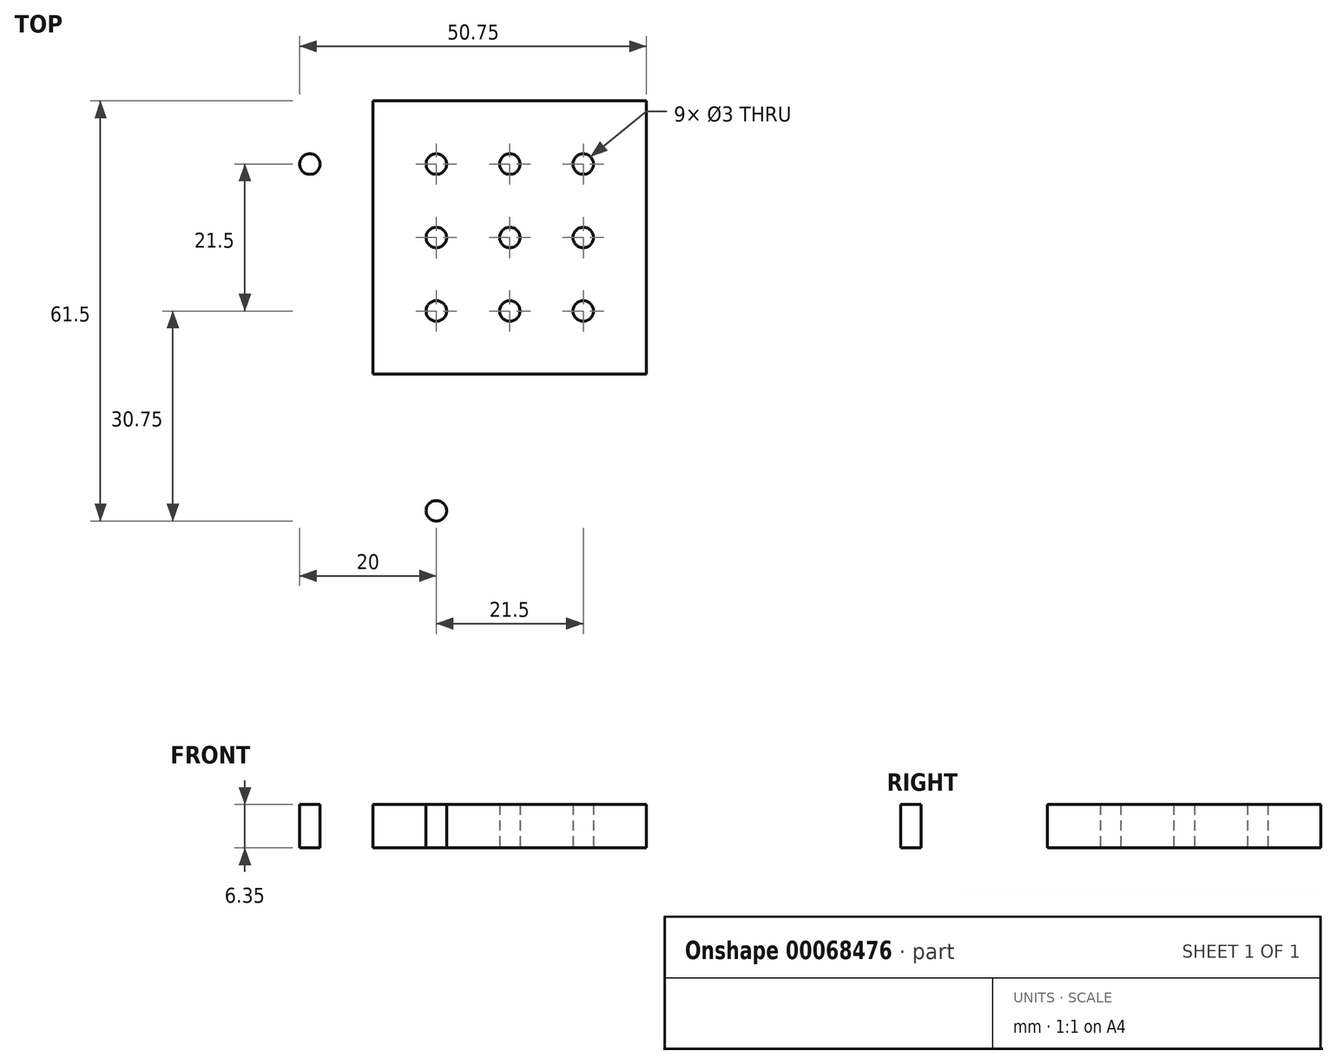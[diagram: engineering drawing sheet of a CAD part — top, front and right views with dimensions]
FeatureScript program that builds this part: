
annotation { "Feature Type Name" : "Feature", "Feature Type Description" : "" }
export const myFeature = defineFeature(function(context is Context, id is Id, definition is map)
    precondition{}
    {
        {
            var Q0;
            Q0=qCreatedBy(makeId("Top.planeOp"),FACE);
            var sketch = newSketch(context, id + "F0", { "sketchPlane" : qUnion([Q0])});
            skLineSegment(sketch, "E0.bottom", {"start": v(9.25, 0) * mm, "end": v(40, 0) * mm});
            skLineSegment(sketch, "E0.top", {"start": v(0, 40) * mm, "end": v(40, 40) * mm});
            skLineSegment(sketch, "E0.left", {"start": v(0, 0) * mm, "end": v(0, 40) * mm});
            skLineSegment(sketch, "E0.right", {"start": v(40, 0) * mm, "end": v(40, 40) * mm});
            skCircle(sketch, "E1", {"center": v(9.25, 30.75) * mm, "radius": 1.5 * mm});
            skCircle(sketch, "E2", {"center": v(20, 30.75) * mm, "radius": 1.5 * mm});
            skCircle(sketch, "E3", {"center": v(30.75, 30.75) * mm, "radius": 1.5 * mm});
            skCircle(sketch, "E4", {"center": v(9.25, 20) * mm, "radius": 1.5 * mm});
            skCircle(sketch, "E5", {"center": v(20, 20) * mm, "radius": 1.5 * mm});
            skCircle(sketch, "E6", {"center": v(30.75, 20) * mm, "radius": 1.5 * mm});
            skCircle(sketch, "E7", {"center": v(9.25, 9.25) * mm, "radius": 1.5 * mm});
            skCircle(sketch, "E8", {"center": v(20, 9.25) * mm, "radius": 1.5 * mm});
            skCircle(sketch, "E9", {"center": v(30.75, 9.25) * mm, "radius": 1.5 * mm});
            skLineSegment(sketch, "E10", {"start": v(0, 30.75) * mm, "end": v(7.75, 30.75) * mm, "construction": true});
            skLineSegment(sketch, "E11", {"start": v(9.25, 40) * mm, "end": v(9.25, 32.25) * mm, "construction": true});
            skLineSegment(sketch, "E12.trimOffspring", {"start": v(9.25, 29.25) * mm, "end": v(9.25, 21.5) * mm, "construction": true});
            skLineSegment(sketch, "E13.trimOffspring", {"start": v(10.75, 30.75) * mm, "end": v(18.5, 30.75) * mm, "construction": true});
            skLineSegment(sketch, "E14.trimOffspring", {"start": v(21.5, 30.75) * mm, "end": v(29.25, 30.75) * mm, "construction": true});
            skLineSegment(sketch, "E15.trimOffspring", {"start": v(32.25, 30.75) * mm, "end": v(40, 30.75) * mm, "construction": true});
            skLineSegment(sketch, "E16.trimOffspring", {"start": v(9.25, 18.5) * mm, "end": v(9.25, 10.75) * mm, "construction": true});
            skLineSegment(sketch, "E17.trimOffspring", {"start": v(9.25, 7.75) * mm, "end": v(9.25, 0) * mm, "construction": true});
            skCircle(sketch, "E18.MirrorC", {"center": v(-9.25, 30.75) * mm, "radius": 1.5 * mm});
            skCircle(sketch, "E19.MirrorC", {"center": v(-9.25, 9.25) * mm, "radius": 1.5 * mm});
            skCircle(sketch, "E20.MirrorC", {"center": v(-30.75, 30.75) * mm, "radius": 1.5 * mm});
            skCircle(sketch, "E21.MirrorC", {"center": v(-20, 30.75) * mm, "radius": 1.5 * mm});
            skCircle(sketch, "E22.MirrorC", {"center": v(-30.75, 9.25) * mm, "radius": 1.5 * mm});
            skCircle(sketch, "E23.MirrorC", {"center": v(-9.25, 20) * mm, "radius": 1.5 * mm});
            skCircle(sketch, "E24.MirrorC", {"center": v(-20, 9.25) * mm, "radius": 1.5 * mm});
            skCircle(sketch, "E25.MirrorC", {"center": v(-30.75, 20) * mm, "radius": 1.5 * mm});
            skCircle(sketch, "E26.MirrorC", {"center": v(-20, 20) * mm, "radius": 1.5 * mm});
            skLineSegment(sketch, "E27.MirrorCS", {"start": v(-10.75, 30.75) * mm, "end": v(-18.5, 30.75) * mm, "construction": true});
            skLineSegment(sketch, "E28.MirrorCS", {"start": v(-32.25, 30.75) * mm, "end": v(-40, 30.75) * mm, "construction": true});
            skLineSegment(sketch, "E29.MirrorCS", {"start": v(0, 30.75) * mm, "end": v(-7.75, 30.75) * mm, "construction": true});
            skLineSegment(sketch, "E30.MirrorCS", {"start": v(-40, 0) * mm, "end": v(-40, 40) * mm});
            skLineSegment(sketch, "E31.MirrorCS", {"start": v(-21.5, 30.75) * mm, "end": v(-29.25, 30.75) * mm, "construction": true});
            skLineSegment(sketch, "E32.MirrorCS", {"start": v(-9.25, 29.25) * mm, "end": v(-9.25, 21.5) * mm, "construction": true});
            skLineSegment(sketch, "E33.MirrorCS", {"start": v(-9.25, 40) * mm, "end": v(-9.25, 32.25) * mm, "construction": true});
            skLineSegment(sketch, "E34.MirrorCS", {"start": v(0, 40) * mm, "end": v(-40, 40) * mm});
            skLineSegment(sketch, "E35.MirrorCS", {"start": v(-9.25, 18.5) * mm, "end": v(-9.25, 10.75) * mm, "construction": true});
            skCircle(sketch, "E36.MirrorC", {"center": v(-9.25, -9.25) * mm, "radius": 1.5 * mm});
            skCircle(sketch, "E37.MirrorC", {"center": v(9.25, -20) * mm, "radius": 1.5 * mm});
            skCircle(sketch, "E38.MirrorC", {"center": v(9.25, -30.75) * mm, "radius": 1.5 * mm});
            skCircle(sketch, "E39.MirrorC", {"center": v(-30.75, -9.25) * mm, "radius": 1.5 * mm});
            skCircle(sketch, "E40.MirrorC", {"center": v(-9.25, -30.75) * mm, "radius": 1.5 * mm});
            skCircle(sketch, "E41.MirrorC", {"center": v(-20, -30.75) * mm, "radius": 1.5 * mm});
            skCircle(sketch, "E42.MirrorC", {"center": v(-30.75, -20) * mm, "radius": 1.5 * mm});
            skCircle(sketch, "E43.MirrorC", {"center": v(-20, -20) * mm, "radius": 1.5 * mm});
            skCircle(sketch, "E44.MirrorC", {"center": v(-30.75, -30.75) * mm, "radius": 1.5 * mm});
            skCircle(sketch, "E45.MirrorC", {"center": v(30.75, -9.25) * mm, "radius": 1.5 * mm});
            skCircle(sketch, "E46.MirrorC", {"center": v(30.75, -30.75) * mm, "radius": 1.5 * mm});
            skCircle(sketch, "E47.MirrorC", {"center": v(20, -20) * mm, "radius": 1.5 * mm});
            skCircle(sketch, "E48.MirrorC", {"center": v(-20, -9.25) * mm, "radius": 1.5 * mm});
            skCircle(sketch, "E49.MirrorC", {"center": v(20, -9.25) * mm, "radius": 1.5 * mm});
            skCircle(sketch, "E50.MirrorC", {"center": v(30.75, -20) * mm, "radius": 1.5 * mm});
            skLineSegment(sketch, "E51.MirrorCS", {"start": v(0, 0) * mm, "end": v(0, -40) * mm, "construction": true});
            skCircle(sketch, "E52.MirrorC", {"center": v(20, -30.75) * mm, "radius": 1.5 * mm});
            skCircle(sketch, "E53.MirrorC", {"center": v(-9.25, -20) * mm, "radius": 1.5 * mm});
            skCircle(sketch, "E54.MirrorC", {"center": v(9.25, -9.25) * mm, "radius": 1.5 * mm});
            skLineSegment(sketch, "E55.MirrorCS", {"start": v(-40, 0) * mm, "end": v(-40, -40) * mm});
            skLineSegment(sketch, "E56.MirrorCS", {"start": v(32.25, -30.75) * mm, "end": v(40, -30.75) * mm, "construction": true});
            skLineSegment(sketch, "E57.MirrorCS", {"start": v(-32.25, -30.75) * mm, "end": v(-40, -30.75) * mm, "construction": true});
            skLineSegment(sketch, "E58.MirrorCS", {"start": v(-9.25, -40) * mm, "end": v(-9.25, -32.25) * mm, "construction": true});
            skLineSegment(sketch, "E59.MirrorCS", {"start": v(21.5, -30.75) * mm, "end": v(29.25, -30.75) * mm, "construction": true});
            skLineSegment(sketch, "E60.MirrorCS", {"start": v(-10.75, -30.75) * mm, "end": v(-18.5, -30.75) * mm, "construction": true});
            skLineSegment(sketch, "E61.MirrorCS", {"start": v(-9.25, -29.25) * mm, "end": v(-9.25, -21.5) * mm, "construction": true});
            skLineSegment(sketch, "E62.MirrorCS", {"start": v(-9.25, -18.5) * mm, "end": v(-9.25, -10.75) * mm, "construction": true});
            skLineSegment(sketch, "E63.MirrorCS", {"start": v(0, -30.75) * mm, "end": v(-7.75, -30.75) * mm, "construction": true});
            skLineSegment(sketch, "E64.MirrorCS", {"start": v(10.75, -30.75) * mm, "end": v(18.5, -30.75) * mm, "construction": true});
            skLineSegment(sketch, "E65.MirrorCS", {"start": v(-21.5, -30.75) * mm, "end": v(-29.25, -30.75) * mm, "construction": true});
            skLineSegment(sketch, "E66.MirrorCS", {"start": v(9.25, -7.75) * mm, "end": v(9.25, 0) * mm, "construction": true});
            skLineSegment(sketch, "E67.MirrorCS", {"start": v(0, -40) * mm, "end": v(-40, -40) * mm});
            skLineSegment(sketch, "E68.MirrorCS", {"start": v(9.25, -40) * mm, "end": v(9.25, -32.25) * mm, "construction": true});
            skLineSegment(sketch, "E69.MirrorCS", {"start": v(9.25, -29.25) * mm, "end": v(9.25, -21.5) * mm, "construction": true});
            skLineSegment(sketch, "E70.MirrorCS", {"start": v(9.25, -18.5) * mm, "end": v(9.25, -10.75) * mm, "construction": true});
            skLineSegment(sketch, "E71.MirrorCS", {"start": v(0, -30.75) * mm, "end": v(7.75, -30.75) * mm, "construction": true});
            skLineSegment(sketch, "E72.MirrorCS", {"start": v(0, 0) * mm, "end": v(40, 0) * mm});
            skLineSegment(sketch, "E73.MirrorCS", {"start": v(0, -40) * mm, "end": v(40, -40) * mm});
            skLineSegment(sketch, "E74.MirrorCS", {"start": v(0, 0) * mm, "end": v(0, -40) * mm});
            skLineSegment(sketch, "E75.MirrorCS", {"start": v(40, 0) * mm, "end": v(40, -40) * mm});
            skPoint(sketch, "E76.MirrorCS.end.orphan", {"position": v(-9.25, 0) * mm});
            skPoint(sketch, "E76.MirrorCS.start.orphan", {"position": v(-9.25, 7.75) * mm});
            skPoint(sketch, "E77.MirrorCS.start.orphan", {"position": v(-9.25, -7.75) * mm});
            skSolve(sketch);
        }
        {
            var Q0;
            Q0=makeQuery(id+"F0.imprint","IMPRINT",FACE,{"disambiguationData":[TD([[makeQuery(id+"F0.imprint","IMPRINT",EDGE,{"derivedFrom":sQuery(id+"F0.wireOp",EDGE,"E0.top")}),-1.0]])]});
            var Q1;
            Q1=makeQuery(id+"F0.imprint","IMPRINT",FACE,{"disambiguationData":[TD([[makeQuery(id+"F0.imprint","IMPRINT",EDGE,{"derivedFrom":sQuery(id+"F0.wireOp",EDGE,"E37.MirrorC")}),1.0]])]});
            var Q2;
            Q2=makeQuery(id+"F0.imprint","IMPRINT",FACE,{"disambiguationData":[TD([[makeQuery(id+"F0.imprint","IMPRINT",EDGE,{"derivedFrom":sQuery(id+"F0.wireOp",EDGE,"E0.top")}),-1.0]])]});
            var Q3;
            Q3=makeQuery(id+"F0.imprint","IMPRINT",FACE,{"disambiguationData":[TD([[makeQuery(id+"F0.imprint","IMPRINT",EDGE,{"derivedFrom":sQuery(id+"F0.wireOp",EDGE,"E37.MirrorC")}),1.0]])]});
            var Q4;
            Q4=makeQuery(id+"F0.imprint","IMPRINT",FACE,{"disambiguationData":[TD([[makeQuery(id+"F0.imprint","IMPRINT",EDGE,{"derivedFrom":sQuery(id+"F0.wireOp",EDGE,"E18.MirrorC")}),1.0]])]});
            extrude(context, id + "F1", {"entities" : qUnion([Q0, Q1, Q2, Q3, Q4]), "depth" : 6.35 * mm});
        }
    });
